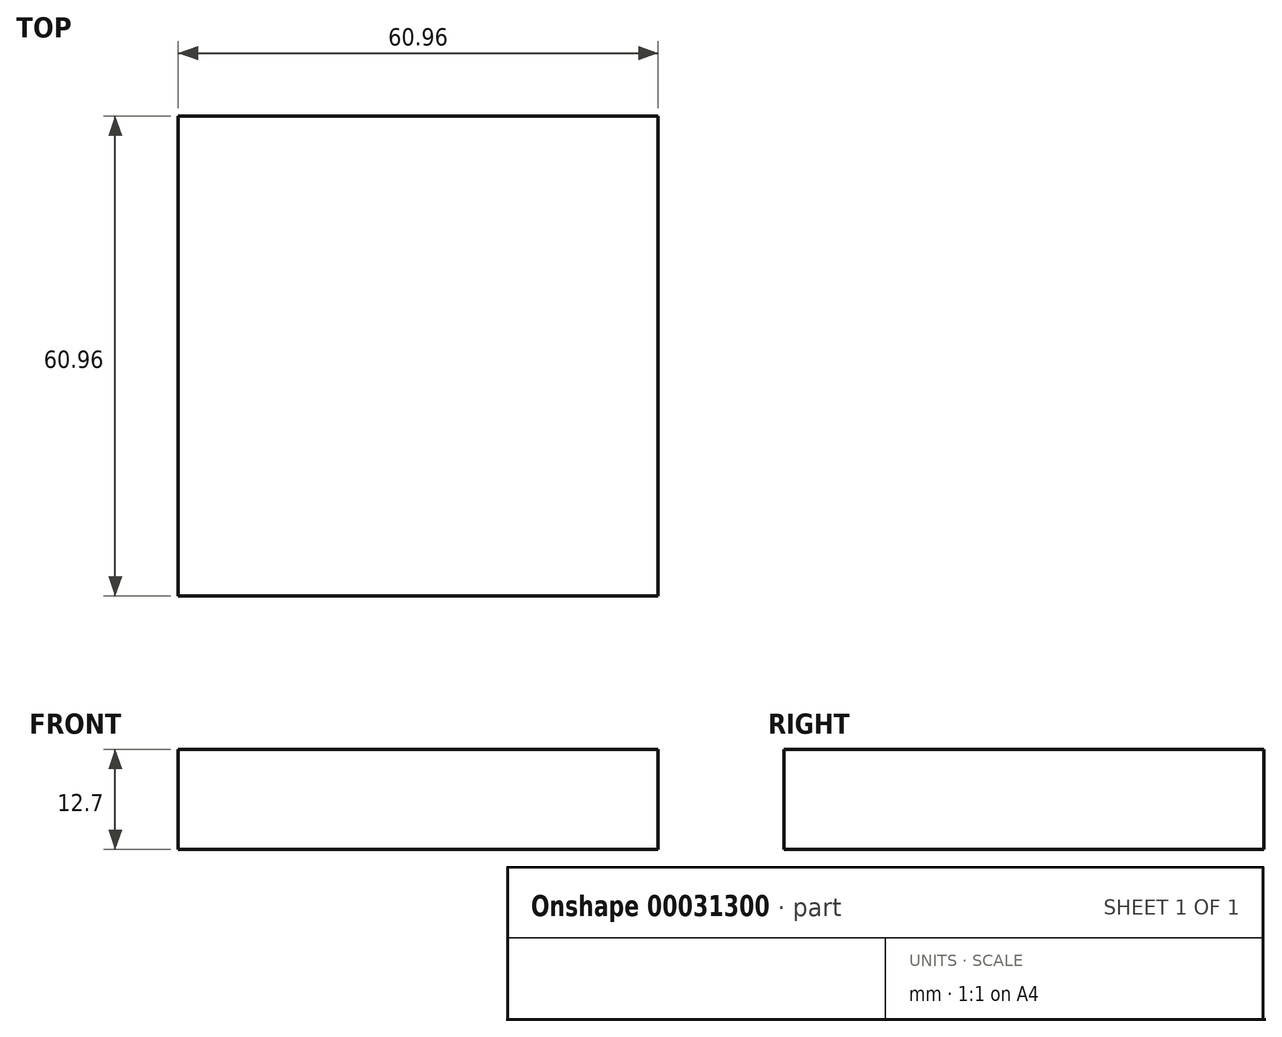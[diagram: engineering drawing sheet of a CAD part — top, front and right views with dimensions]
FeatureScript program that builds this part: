
annotation { "Feature Type Name" : "Feature", "Feature Type Description" : "" }
export const myFeature = defineFeature(function(context is Context, id is Id, definition is map)
    precondition{}
    {
        {
            var Q0;
            Q0=qCreatedBy(makeId("Top.planeOp"),FACE);
            var sketch = newSketch(context, id + "F0", { "sketchPlane" : qUnion([Q0])});
            skLineSegment(sketch, "E0.bottom", {"start": v(0, 0) * mm, "end": v(60.96, 0) * mm});
            skLineSegment(sketch, "E0.top", {"start": v(0, -60.96) * mm, "end": v(60.96, -60.96) * mm});
            skLineSegment(sketch, "E0.left", {"start": v(0, 0) * mm, "end": v(0, -60.96) * mm});
            skLineSegment(sketch, "E0.right", {"start": v(60.96, 0) * mm, "end": v(60.96, -60.96) * mm});
            skSolve(sketch);
        }
        {
            var Q0;
            Q0=makeQuery(id+"F0.imprint","IMPRINT",FACE,{"disambiguationData":[TD([[makeQuery(id+"F0.imprint","IMPRINT",EDGE,{"derivedFrom":sQuery(id+"F0.wireOp",EDGE,"E0.bottom")}),-1.0]])]});
            extrude(context, id + "F1", {"entities" : qUnion([Q0]), "depth" : 12.7 * mm});
        }
    });
